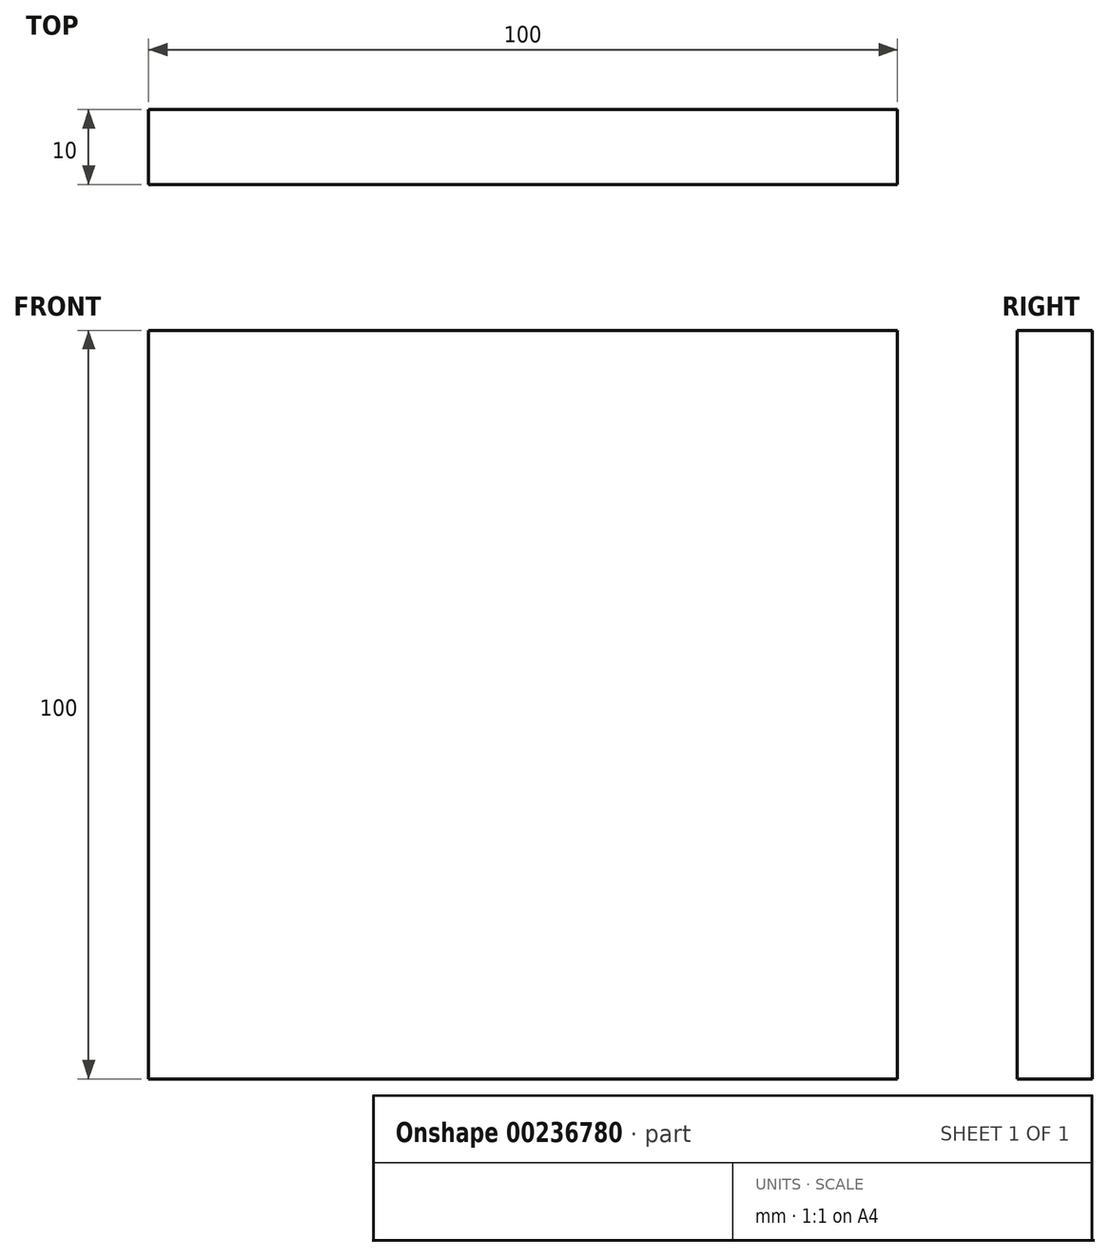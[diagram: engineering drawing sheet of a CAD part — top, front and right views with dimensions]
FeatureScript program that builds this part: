
annotation { "Feature Type Name" : "Feature", "Feature Type Description" : "" }
export const myFeature = defineFeature(function(context is Context, id is Id, definition is map)
    precondition{}
    {
        {
            var Q0;
            Q0=qCreatedBy(makeId("Front.planeOp"),FACE);
            var sketch = newSketch(context, id + "F0", { "sketchPlane" : qUnion([Q0])});
            skLineSegment(sketch, "E0.bottom", {"start": v(0, 0) * mm, "end": v(100, 0) * mm});
            skLineSegment(sketch, "E0.top", {"start": v(0, 100) * mm, "end": v(100, 100) * mm});
            skLineSegment(sketch, "E0.left", {"start": v(0, 0) * mm, "end": v(0, 100) * mm});
            skLineSegment(sketch, "E0.right", {"start": v(100, 0) * mm, "end": v(100, 100) * mm});
            skSolve(sketch);
        }
        {
            var Q0;
            Q0=makeQuery(id+"F0.imprint","IMPRINT",FACE,{"disambiguationData":[TD([[makeQuery(id+"F0.imprint","IMPRINT",EDGE,{"derivedFrom":sQuery(id+"F0.wireOp",EDGE,"E0.bottom")}),1.0]])]});
            extrude(context, id + "F1", {"entities" : qUnion([Q0]), "depth" : 10 * mm, "offsetDistance" : 25 * mm});
        }
    });
